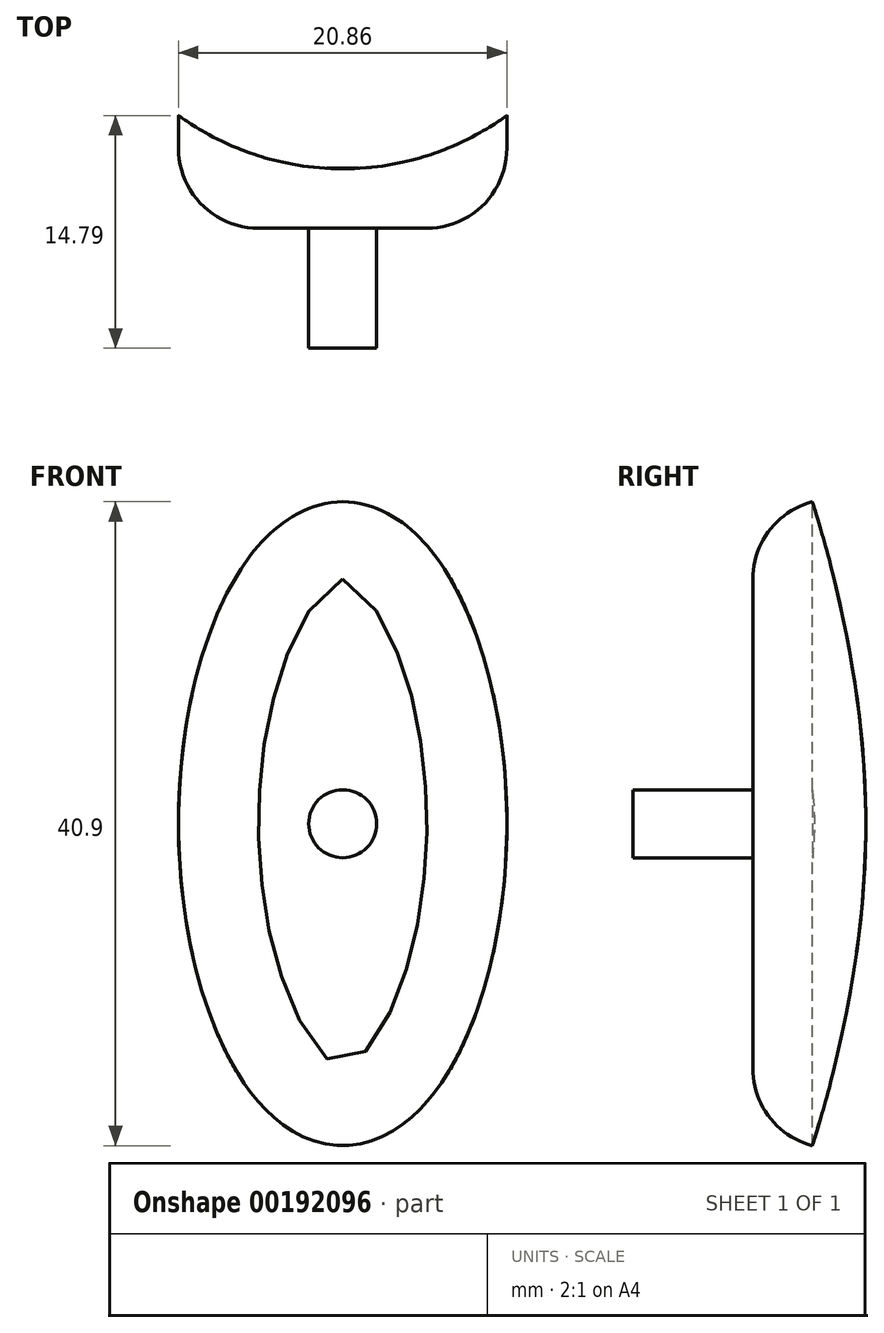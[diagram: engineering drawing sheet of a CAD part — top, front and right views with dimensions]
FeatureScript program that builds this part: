
annotation { "Feature Type Name" : "Feature", "Feature Type Description" : "" }
export const myFeature = defineFeature(function(context is Context, id is Id, definition is map)
    precondition{}
    {
        {
            var Q0;
            Q0=qCreatedBy(makeId("Front.planeOp"),FACE);
            var sketch = newSketch(context, id + "F0", { "sketchPlane" : qUnion([Q0])});
            skEllipse(sketch, "E0", {"center": v(0, 0) * mm, "majorRadius": 20.62 * mm, "minorRadius": 10.43 * mm, "majorAxis": v(0, 1)});
            skCircle(sketch, "E1", {"center": v(0, 0) * mm, "radius": 2.16 * mm});
            skSolve(sketch);
        }
        {
            var Q0;
            Q0=makeQuery(id+"F0.imprint","IMPRINT",FACE,{"disambiguationData":[TD([[makeQuery(id+"F0.imprint","IMPRINT",EDGE,{"derivedFrom":sQuery(id+"F0.wireOp",EDGE,"E1")}),1.0]])]});
            extrude(context, id + "F1", {"entities" : qUnion([Q0]), "depth" : 7.62 * mm});
        }
        {
            var Q0;
            Q0=makeQuery(id+"F0.imprint","IMPRINT",FACE,{"disambiguationData":[TD([[makeQuery(id+"F0.imprint","IMPRINT",EDGE,{"derivedFrom":sQuery(id+"F0.wireOp",EDGE,"E0")}),1.0]])]});
            extrude(context, id + "F2", {"entities" : qUnion([Q0]), "oppositeDirection" : true, "depth" : 10.16 * mm});
        }
        {
            var Q0;
            Q0=qCreatedBy(makeId("Top.planeOp"),FACE);
            var sketch = newSketch(context, id + "F3", { "sketchPlane" : qUnion([Q0])});
            skCircle(sketch, "E2", {"center": v(0, 21.48) * mm, "radius": 17.7 * mm});
            skSolve(sketch);
        }
        {
            var Q0;
            Q0=makeQuery(id+"F3.imprint","IMPRINT",FACE,{"disambiguationData":[TD([[makeQuery(id+"F3.imprint","IMPRINT",EDGE,{"derivedFrom":sQuery(id+"F3.wireOp",EDGE,"E2")}),1.0]])]});
            extrude(context, id + "F4", {"entities" : qUnion([Q0]), "operationType" : NewBodyOperationType.REMOVE, "endBound" : BoundingType.SYMMETRIC, "oppositeDirection" : true, "depth" : 50.8 * mm});
        }
        {
            var Q0;
            Q0=makeQuery(id+"F0.imprint","IMPRINT",FACE,{"disambiguationData":[TD([[makeQuery(id+"F0.imprint","IMPRINT",EDGE,{"derivedFrom":sQuery(id+"F0.wireOp",EDGE,"E1")}),1.0]])]});
            extrude(context, id + "F5", {"entities" : qUnion([Q0]), "operationType" : NewBodyOperationType.ADD, "oppositeDirection" : true, "depth" : 3.8 * mm});
        }
        {
            var Q0;
            Q0=makeQuery(id+"F2.opExtrude","CAP_EDGE",EDGE,{"disambiguationData":[OSD([sQuery(id+"F0.wireOp",EDGE,"E0")])],"isStart":true});
            fillet(context, id + "F6", {"entities" : qUnion([Q0]), "radius" : 5.08 * mm, "tangentPropagation" : true, "allowEdgeOverflow" : false});
        }
    });
